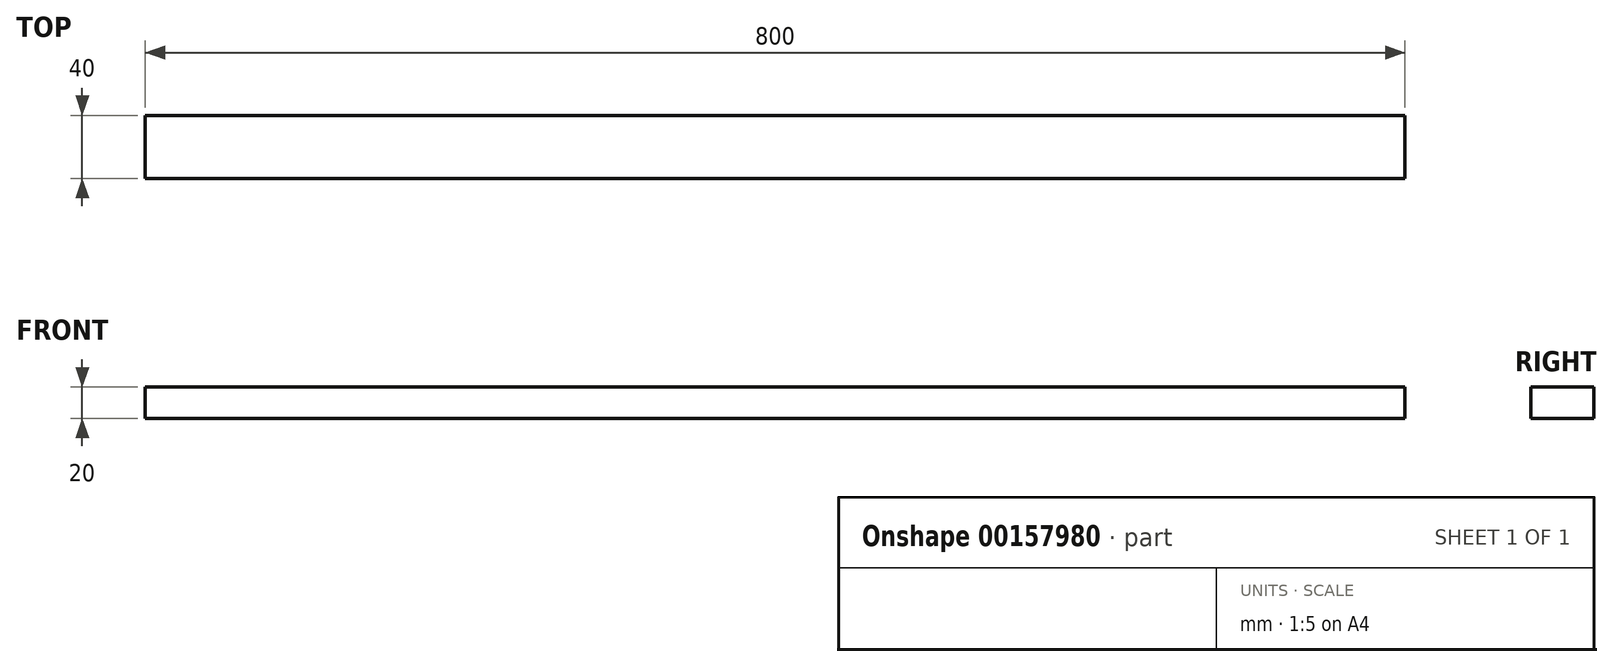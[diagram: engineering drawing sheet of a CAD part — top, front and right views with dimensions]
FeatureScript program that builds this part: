
annotation { "Feature Type Name" : "Feature", "Feature Type Description" : "" }
export const myFeature = defineFeature(function(context is Context, id is Id, definition is map)
    precondition{}
    {
        {
            var Q0;
            Q0=qCreatedBy(makeId("Top.planeOp"),FACE);
            var sketch = newSketch(context, id + "F0", { "sketchPlane" : qUnion([Q0])});
            skLineSegment(sketch, "E0.bottom", {"start": v(-400, -20) * mm, "end": v(400, -20) * mm});
            skLineSegment(sketch, "E0.top", {"start": v(-400, 20) * mm, "end": v(400, 20) * mm});
            skLineSegment(sketch, "E0.left", {"start": v(-400, -20) * mm, "end": v(-400, 20) * mm});
            skLineSegment(sketch, "E0.right", {"start": v(400, -20) * mm, "end": v(400, 20) * mm});
            skPoint(sketch, "E0.middle", {"position": v(0, 0) * mm});
            skSolve(sketch);
        }
        {
            var Q0;
            Q0=qSketchRegion(id+"F0",true);
            extrude(context, id + "F1", {"entities" : qUnion([Q0]), "endBound" : BoundingType.SYMMETRIC, "depth" : 20 * mm});
        }
    });
